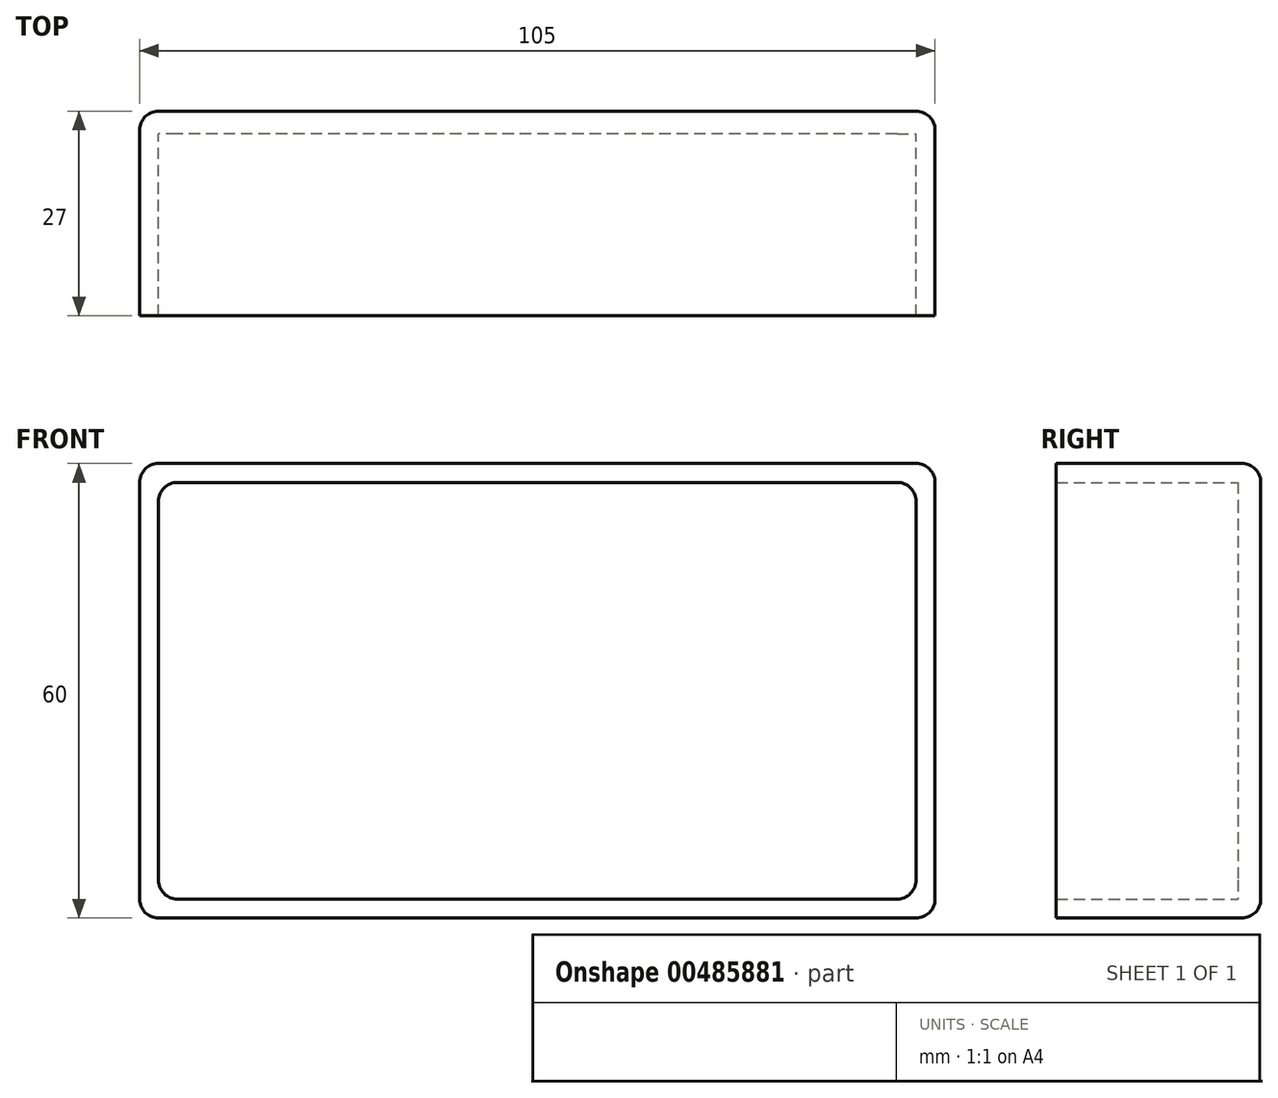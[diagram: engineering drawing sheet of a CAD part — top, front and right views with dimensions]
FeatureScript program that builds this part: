
annotation { "Feature Type Name" : "Feature", "Feature Type Description" : "" }
export const myFeature = defineFeature(function(context is Context, id is Id, definition is map)
    precondition{}
    {
        {
            var Q0;
            Q0=qCreatedBy(makeId("Front.planeOp"),FACE);
            var sketch = newSketch(context, id + "F0", { "sketchPlane" : qUnion([Q0])});
            skLineSegment(sketch, "E0.bottom", {"start": v(50, 27.5) * mm, "end": v(-50, 27.5) * mm});
            skLineSegment(sketch, "E0.top", {"start": v(50, -27.5) * mm, "end": v(-50, -27.5) * mm});
            skLineSegment(sketch, "E0.left", {"start": v(50, 27.5) * mm, "end": v(50, -27.5) * mm});
            skLineSegment(sketch, "E0.right", {"start": v(-50, 27.5) * mm, "end": v(-50, -27.5) * mm});
            skPoint(sketch, "E0.middle", {"position": v(0, 0) * mm});
            skLineSegment(sketch, "E1.bottom", {"start": v(-52.5, 30) * mm, "end": v(52.5, 30) * mm});
            skLineSegment(sketch, "E1.top", {"start": v(-52.5, -30) * mm, "end": v(52.5, -30) * mm});
            skLineSegment(sketch, "E1.left", {"start": v(-52.5, 30) * mm, "end": v(-52.5, -30) * mm});
            skLineSegment(sketch, "E1.right", {"start": v(52.5, 30) * mm, "end": v(52.5, -30) * mm});
            skSolve(sketch);
        }
        {
            var Q0;
            Q0=qCreatedBy(makeId("Front.planeOp"),FACE);
            var sketch = newSketch(context, id + "F1", { "sketchPlane" : qUnion([Q0])});
            skLineSegment(sketch, "E2.bottom", {"start": v(-43, -22) * mm, "end": v(43, -22) * mm, "construction": true});
            skLineSegment(sketch, "E2.top", {"start": v(-43, 22) * mm, "end": v(43, 22) * mm, "construction": true});
            skLineSegment(sketch, "E2.left", {"start": v(-43, -22) * mm, "end": v(-43, 22) * mm, "construction": true});
            skLineSegment(sketch, "E2.right", {"start": v(43, -22) * mm, "end": v(43, 22) * mm, "construction": true});
            skPoint(sketch, "E2.middle", {"position": v(0, 0) * mm});
            skCircle(sketch, "E3", {"center": v(-43, 22) * mm, "radius": 1.25 * mm});
            skCircle(sketch, "E4", {"center": v(-43, 22) * mm, "radius": 3 * mm});
            skCircle(sketch, "E5", {"center": v(-43, -22) * mm, "radius": 1.25 * mm});
            skCircle(sketch, "E6", {"center": v(-43, -22) * mm, "radius": 3 * mm});
            skCircle(sketch, "E7", {"center": v(43, -22) * mm, "radius": 1.25 * mm});
            skCircle(sketch, "E8", {"center": v(43, -22) * mm, "radius": 3 * mm});
            skCircle(sketch, "E9", {"center": v(43, 22) * mm, "radius": 1.25 * mm});
            skCircle(sketch, "E10", {"center": v(43, 22) * mm, "radius": 3 * mm});
            skLineSegment(sketch, "E11.bottom", {"start": v(-43, -22) * mm, "end": v(-34.5, -22) * mm, "construction": true});
            skLineSegment(sketch, "E11.top", {"start": v(-43, -31.15) * mm, "end": v(-34.5, -31.15) * mm, "construction": true});
            skLineSegment(sketch, "E11.left", {"start": v(-43, -22) * mm, "end": v(-43, -31.15) * mm, "construction": true});
            skLineSegment(sketch, "E11.right", {"start": v(-34.5, -22) * mm, "end": v(-34.5, -31.15) * mm, "construction": true});
            skSolve(sketch);
        }
        {
            var Q0;
            Q0=makeQuery(id+"F0.imprint","IMPRINT",FACE,{"disambiguationData":[TD([[makeQuery(id+"F0.imprint","IMPRINT",EDGE,{"derivedFrom":sQuery(id+"F0.wireOp",EDGE,"E0.bottom")}),-1.0]])]});
            extrude(context, id + "F2", {"entities" : qUnion([Q0]), "depth" : 24 * mm});
        }
        {
            var Q0;
            Q0=makeQuery(id+"F0.imprint","IMPRINT",FACE,{"disambiguationData":[TD([[makeQuery(id+"F0.imprint","IMPRINT",EDGE,{"derivedFrom":sQuery(id+"F0.wireOp",EDGE,"E0.bottom")}),1.0]])]});
            var Q1;
            Q1=makeQuery(id+"F2.opExtrude","CAP_FACE",FACE,{"disambiguationData":[OSD([sQuery(id+"F0.wireOp",EDGE,"E0.bottom"),sQuery(id+"F0.wireOp",EDGE,"E0.top"),sQuery(id+"F0.wireOp",EDGE,"E0.left"),sQuery(id+"F0.wireOp",EDGE,"E0.right"),sQuery(id+"F0.wireOp",EDGE,"E1.bottom"),sQuery(id+"F0.wireOp",EDGE,"E1.top"),sQuery(id+"F0.wireOp",EDGE,"E1.left"),sQuery(id+"F0.wireOp",EDGE,"E1.right")])],"isStart":false});
            var Q2;
            Q2=makeQuery(id+"F1.imprint","IMPRINT",FACE,{"disambiguationData":[TD([[makeQuery(id+"F1.imprint","IMPRINT",EDGE,{"derivedFrom":sQuery(id+"F1.wireOp",EDGE,"E5")}),-1.0]])]});
            var Q3;
            Q3=makeQuery(id+"F1.imprint","IMPRINT",FACE,{"disambiguationData":[TD([[makeQuery(id+"F1.imprint","IMPRINT",EDGE,{"derivedFrom":sQuery(id+"F1.wireOp",EDGE,"E3")}),-1.0]])]});
            var Q4;
            Q4=makeQuery(id+"F1.imprint","IMPRINT",FACE,{"disambiguationData":[TD([[makeQuery(id+"F1.imprint","IMPRINT",EDGE,{"derivedFrom":sQuery(id+"F1.wireOp",EDGE,"E9")}),-1.0]])]});
            var Q5;
            Q5=makeQuery(id+"F1.imprint","IMPRINT",FACE,{"disambiguationData":[TD([[makeQuery(id+"F1.imprint","IMPRINT",EDGE,{"derivedFrom":sQuery(id+"F1.wireOp",EDGE,"E7")}),-1.0]])]});
            extrude(context, id + "F3", {"entities" : qUnion([Q0, Q1, Q2, Q3, Q4, Q5]), "operationType" : NewBodyOperationType.ADD, "depth" : 3 * mm});
        }
        {
            var Q0;
            {var subQ0=sQuery(id+"F0.wireOp",EDGE,"E1.left");var subQ1=sQuery(id+"F0.wireOp",EDGE,"E1.top");Q0=makeQuery(id+"F3.boolean.opBoolean","MERGE",EDGE,{"derivedFrom":[makeQuery(id+"F2.opExtrude","SWEPT_EDGE",EDGE,{"disambiguationData":[OSD([subQ1,subQ0])]}),makeQuery(id+"F3.opExtrude","SWEPT_EDGE",EDGE,{"disambiguationData":[OSD([subQ1,subQ0])]})]});}
            var Q1;
            {var subQ0=sQuery(id+"F0.wireOp",EDGE,"E1.right");var subQ1=sQuery(id+"F0.wireOp",EDGE,"E1.top");Q1=makeQuery(id+"F3.boolean.opBoolean","MERGE",EDGE,{"derivedFrom":[makeQuery(id+"F2.opExtrude","SWEPT_EDGE",EDGE,{"disambiguationData":[OSD([subQ1,subQ0])]}),makeQuery(id+"F3.opExtrude","SWEPT_EDGE",EDGE,{"disambiguationData":[OSD([subQ1,subQ0])]})]});}
            var Q2;
            {var subQ0=sQuery(id+"F0.wireOp",EDGE,"E1.right");var subQ1=sQuery(id+"F0.wireOp",EDGE,"E1.bottom");Q2=makeQuery(id+"F3.boolean.opBoolean","MERGE",EDGE,{"derivedFrom":[makeQuery(id+"F2.opExtrude","SWEPT_EDGE",EDGE,{"disambiguationData":[OSD([subQ1,subQ0])]}),makeQuery(id+"F3.opExtrude","SWEPT_EDGE",EDGE,{"disambiguationData":[OSD([subQ1,subQ0])]})]});}
            var Q3;
            {var subQ0=sQuery(id+"F0.wireOp",EDGE,"E1.left");var subQ1=sQuery(id+"F0.wireOp",EDGE,"E1.bottom");Q3=makeQuery(id+"F3.boolean.opBoolean","MERGE",EDGE,{"derivedFrom":[makeQuery(id+"F2.opExtrude","SWEPT_EDGE",EDGE,{"disambiguationData":[OSD([subQ1,subQ0])]}),makeQuery(id+"F3.opExtrude","SWEPT_EDGE",EDGE,{"disambiguationData":[OSD([subQ1,subQ0])]})]});}
            var Q4;
            Q4=makeQuery(id+"F2.opExtrude","CAP_EDGE",EDGE,{"disambiguationData":[OSD([sQuery(id+"F0.wireOp",EDGE,"E1.bottom")])],"isStart":true});
            var Q5;
            Q5=makeQuery(id+"F2.opExtrude","CAP_EDGE",EDGE,{"disambiguationData":[OSD([sQuery(id+"F0.wireOp",EDGE,"E1.left")])],"isStart":true});
            var Q6;
            Q6=makeQuery(id+"F2.opExtrude","CAP_EDGE",EDGE,{"disambiguationData":[OSD([sQuery(id+"F0.wireOp",EDGE,"E1.top")])],"isStart":true});
            var Q7;
            Q7=makeQuery(id+"F2.opExtrude","CAP_EDGE",EDGE,{"disambiguationData":[OSD([sQuery(id+"F0.wireOp",EDGE,"E1.right")])],"isStart":true});
            var Q8;
            {var subQ0=sQuery(id+"F0.wireOp",EDGE,"E0.left");var subQ1=sQuery(id+"F0.wireOp",EDGE,"E0.top");Q8=makeQuery(id+"F3.boolean.opBoolean","MERGE",EDGE,{"derivedFrom":[makeQuery(id+"F2.opExtrude","SWEPT_EDGE",EDGE,{"disambiguationData":[OSD([subQ1,subQ0])]}),makeQuery(id+"F3.opExtrude","SWEPT_EDGE",EDGE,{"disambiguationData":[OSD([subQ1,subQ0]),TDD([makeQuery(id+"F2.opExtrude","CAP_VERTEX",VERTEX,{"disambiguationData":[OSD([subQ1,subQ0])],"isStart":false})])]})]});}
            var Q9;
            {var subQ0=sQuery(id+"F0.wireOp",EDGE,"E0.right");var subQ1=sQuery(id+"F0.wireOp",EDGE,"E0.top");Q9=makeQuery(id+"F3.boolean.opBoolean","MERGE",EDGE,{"derivedFrom":[makeQuery(id+"F2.opExtrude","SWEPT_EDGE",EDGE,{"disambiguationData":[OSD([subQ1,subQ0])]}),makeQuery(id+"F3.opExtrude","SWEPT_EDGE",EDGE,{"disambiguationData":[OSD([subQ1,subQ0]),TDD([makeQuery(id+"F2.opExtrude","CAP_VERTEX",VERTEX,{"disambiguationData":[OSD([subQ1,subQ0])],"isStart":false})])]})]});}
            var Q10;
            {var subQ0=sQuery(id+"F0.wireOp",EDGE,"E0.left");var subQ1=sQuery(id+"F0.wireOp",EDGE,"E0.bottom");Q10=makeQuery(id+"F3.boolean.opBoolean","MERGE",EDGE,{"derivedFrom":[makeQuery(id+"F2.opExtrude","SWEPT_EDGE",EDGE,{"disambiguationData":[OSD([subQ1,subQ0])]}),makeQuery(id+"F3.opExtrude","SWEPT_EDGE",EDGE,{"disambiguationData":[OSD([subQ1,subQ0]),TDD([makeQuery(id+"F2.opExtrude","CAP_VERTEX",VERTEX,{"disambiguationData":[OSD([subQ1,subQ0])],"isStart":false})])]})]});}
            var Q11;
            {var subQ0=sQuery(id+"F0.wireOp",EDGE,"E0.right");var subQ1=sQuery(id+"F0.wireOp",EDGE,"E0.bottom");Q11=makeQuery(id+"F3.boolean.opBoolean","MERGE",EDGE,{"derivedFrom":[makeQuery(id+"F2.opExtrude","SWEPT_EDGE",EDGE,{"disambiguationData":[OSD([subQ1,subQ0])]}),makeQuery(id+"F3.opExtrude","SWEPT_EDGE",EDGE,{"disambiguationData":[OSD([subQ1,subQ0]),TDD([makeQuery(id+"F2.opExtrude","CAP_VERTEX",VERTEX,{"disambiguationData":[OSD([subQ1,subQ0])],"isStart":false})])]})]});}
            fillet(context, id + "F4", {"entities" : qUnion([Q0, Q1, Q2, Q3, Q4, Q5, Q6, Q7, Q8, Q9, Q10, Q11]), "radius" : 2.5 * mm, "tangentPropagation" : true, "allowEdgeOverflow" : false});
        }
    });
